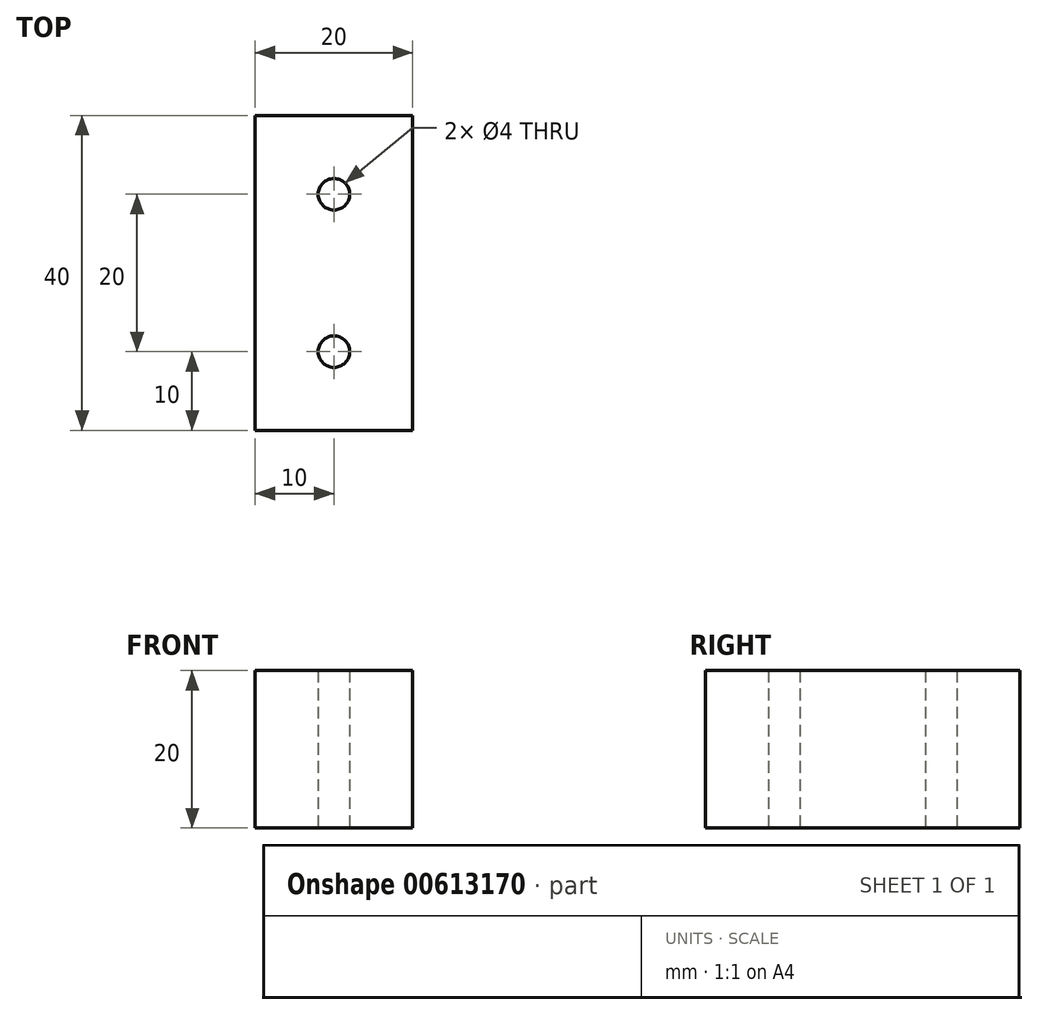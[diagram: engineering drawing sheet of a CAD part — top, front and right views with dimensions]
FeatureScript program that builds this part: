
annotation { "Feature Type Name" : "Feature", "Feature Type Description" : "" }
export const myFeature = defineFeature(function(context is Context, id is Id, definition is map)
    precondition{}
    {
        {
            var Q0;
            Q0=qCreatedBy(makeId("Top.planeOp"),FACE);
            var sketch = newSketch(context, id + "F0", { "sketchPlane" : qUnion([Q0])});
            skLineSegment(sketch, "E0.bottom", {"start": v(10, 20) * mm, "end": v(-10, 20) * mm});
            skLineSegment(sketch, "E0.top", {"start": v(10, -20) * mm, "end": v(-10, -20) * mm});
            skLineSegment(sketch, "E0.left", {"start": v(10, 20) * mm, "end": v(10, -20) * mm});
            skLineSegment(sketch, "E0.right", {"start": v(-10, 20) * mm, "end": v(-10, -20) * mm});
            skPoint(sketch, "E0.middle", {"position": v(0, 0) * mm});
            skSolve(sketch);
        }
        {
            var Q0;
            Q0=qSketchRegion(id+"F0",true);
            extrude(context, id + "F1", {"entities" : qUnion([Q0]), "depth" : 20 * mm, "offsetDistance" : 25 * mm});
        }
        {
            var Q0;
            Q0=makeQuery(id+"F1.opExtrude","CAP_FACE",FACE,{"disambiguationData":[OSD([sQuery(id+"F0.wireOp",EDGE,"E0.bottom"),sQuery(id+"F0.wireOp",EDGE,"E0.top"),sQuery(id+"F0.wireOp",EDGE,"E0.left"),sQuery(id+"F0.wireOp",EDGE,"E0.right")])],"isStart":true});
            var sketch = newSketch(context, id + "F2", { "sketchPlane" : qUnion([Q0])});
            skCircle(sketch, "E1", {"center": v(0, 10) * mm, "radius": 2 * mm});
            skCircle(sketch, "E2", {"center": v(0, -10) * mm, "radius": 2 * mm});
            skSolve(sketch);
        }
        {
            var Q0;
            Q0=qSketchRegion(id+"F2",true);
            extrude(context, id + "F3", {"entities" : qUnion([Q0]), "operationType" : NewBodyOperationType.REMOVE, "oppositeDirection" : true, "depth" : 30 * mm, "offsetDistance" : 25 * mm});
        }
        {
            var Q0;
            Q0=makeQuery(id+"F1.opExtrude","CAP_FACE",FACE,{"disambiguationData":[OSD([sQuery(id+"F0.wireOp",EDGE,"E0.bottom"),sQuery(id+"F0.wireOp",EDGE,"E0.top"),sQuery(id+"F0.wireOp",EDGE,"E0.left"),sQuery(id+"F0.wireOp",EDGE,"E0.right")])],"isStart":false});
            var sketch = newSketch(context, id + "F4", { "sketchPlane" : qUnion([Q0])});
            skCircle(sketch, "E3", {"center": v(0, 10) * mm, "radius": 2 * mm});
            skCircle(sketch, "E4", {"center": v(0, -10) * mm, "radius": 2 * mm});
            skSolve(sketch);
        }
        {
            var Q0;
            Q0=qSketchRegion(id+"F4",true);
            extrude(context, id + "F5", {"entities" : qUnion([Q0]), "operationType" : NewBodyOperationType.REMOVE, "oppositeDirection" : true, "depth" : 30 * mm, "offsetDistance" : 25 * mm});
        }
    });
